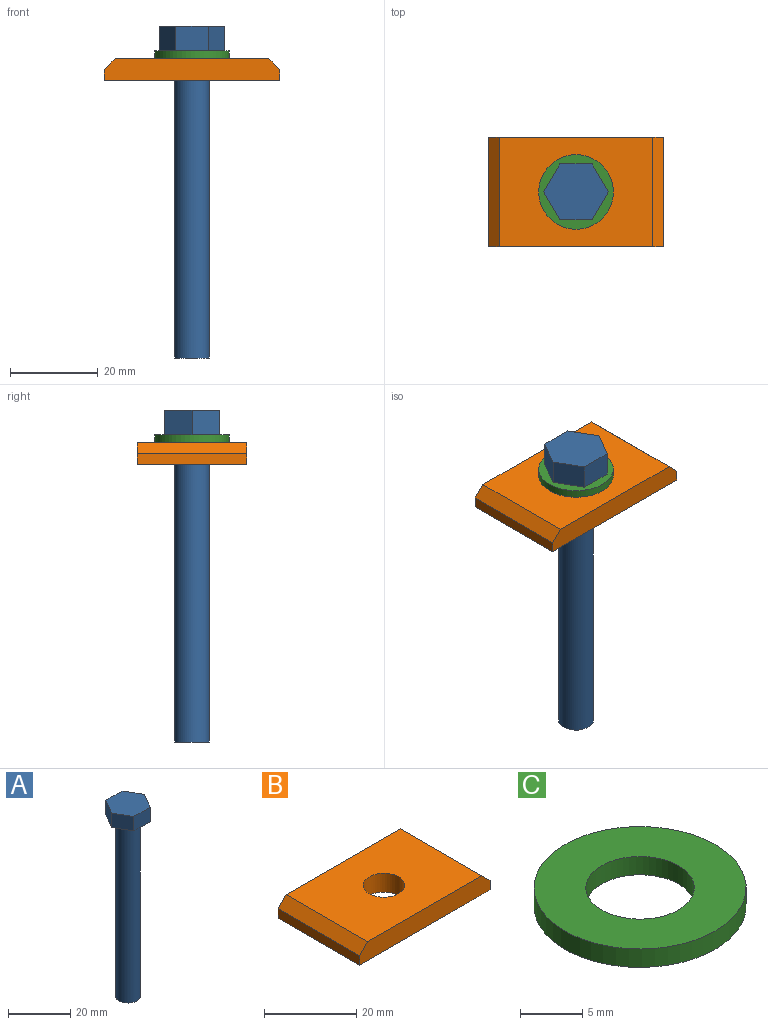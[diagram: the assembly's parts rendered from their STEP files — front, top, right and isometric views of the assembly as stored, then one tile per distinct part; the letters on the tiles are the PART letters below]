
ASSEMBLY  parts=3 mates=4
PART A: 10 faces, bbox 14.7x12.8x75.7 mm
  f0: cylinder r=3.99mm len=70mm, axis (0,0,-1), area 1753.8mm2, adj f1,f9
  f1: plane 7.98x7.98mm, normal (0,0,-1), area 50mm2, adj f0
  f2: plane 6.38x5.65mm, normal (-0.87,0.5,0), area 41.6mm2, adj f3,f7,f8,f9
  f3: plane 6.38x5.65mm, normal (-0.87,-0.5,0), area 41.6mm2, adj f2,f4,f8,f9
  f4: plane 7.36x5.65mm, normal (0,-1,0), area 41.6mm2, adj f3,f5,f8,f9
  f5: plane 6.38x5.65mm, normal (0.87,-0.5,0), area 41.6mm2, adj f4,f6,f8,f9
  f6: plane 6.38x5.65mm, normal (0.87,0.5,0), area 41.6mm2, adj f5,f7,f8,f9
  f7: plane 7.36x5.65mm, normal (0,1,0), area 41.6mm2, adj f2,f6,f8,f9
  f8: plane 14.72x12.75mm, normal (0,0,1), area 140.8mm2, adj f2,f3,f4,f5,f6,f7
  f9: plane 14.72x12.75mm, normal (0,0,-1), area 90.8mm2, adj f0,f2,f3,f4,f5,f6,f7
PART B: 9 faces, bbox 40x25x5 mm
  f0: plane 35x25mm, normal (0,0,1), area 811.4mm2, adj f1,f5,f6,f7,f8
  f1: plane 25x2.5mm, normal (-0.71,0,0.71), area 88.4mm2, adj f0,f2,f6,f7
  f2: plane 25x2.5mm, normal (-1,0,0), area 62.5mm2, adj f1,f3,f6,f7
  f3: plane 40x25mm, normal (0,0,-1), area 936.4mm2, adj f2,f4,f6,f7,f8
  f4: plane 25x2.5mm, normal (1,0,0), area 62.5mm2, adj f3,f5,f6,f7
  f5: plane 25x2.5mm, normal (0.71,0,0.71), area 88.4mm2, adj f0,f4,f6,f7
  f6: plane 40x5mm, normal (0,-1,0), area 193.7mm2, adj f0,f1,f2,f3,f4,f5
  f7: plane 40x5mm, normal (0,1,0), area 193.7mm2, adj f0,f1,f2,f3,f4,f5
  f8: cylinder r=4.5mm len=9mm, axis (0,0,1), area 141.4mm2, adj f0,f3
PART C: 4 faces, bbox 17x17x1.8 mm
  f0: cylinder r=4.35mm len=8.7mm, axis (0,0,-1), area 49.2mm2, adj f2,f3
  f1: cylinder r=8.5mm len=17mm, axis (0,0,-1), area 96.1mm2, adj f2,f3
  f2: plane 17x17mm, normal (0,0,1), area 167.5mm2, adj f0,f1
  f3: plane 17x17mm, normal (0,0,-1), area 167.5mm2, adj f0,f1
PLACE A t=(0.51,-0.36,-141.68)mm
PLACE B t=(0.51,-0.36,1.52)mm fixed
PLACE C t=(0.51,-0.36,51.52)mm
MATE cylindrical C.f0 <-> A.f0  axis (0,0,-1) through (0.51,-0.36,3.32)mm
MATE planar C.f0 <-> A.f0  axis (0,0,1) through (0.51,-0.36,3.32)mm
MATE planar B.f8 <-> C.f0  axis (0,0,1) through (0.51,-0.36,1.52)mm
MATE cylindrical A.f0 <-> B.f8  axis (0,0,-1) through (0.51,-0.36,-31.68)mm
